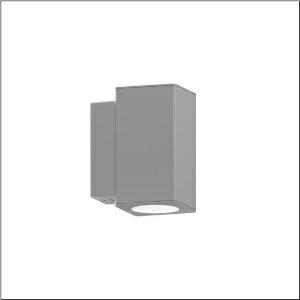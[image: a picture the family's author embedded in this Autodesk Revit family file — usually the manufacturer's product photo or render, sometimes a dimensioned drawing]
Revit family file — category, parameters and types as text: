
# Revit family: cl_31_wand_5cl563623
name_source: partatom
category: Lighting Fixtures
units: mm (PartAtom-declared; Revit-internal decimal feet)

## family parameters
Cut with Voids When Loaded = No
Host = Face
Light Source = No
Part Type = Normal
Room Calculation Point = No
Round Connector Dimension = Use Diameter
Shared = No

## types (1)
- --- (1 x LED, 600 lm, 5.4 W, 3000K)
    Apparent Load = 5 VA
    CIE Flux Codes = 98 100 100 50 100
    Color Rendering = 80
    Color Temperature = 3000K
    Default Elevation = 1800 mm
    Description = CL 31 Wall, wall luminaire, primary light control with reflector, of aluminium, primary optical cover: cover panel, of glass, transparent, light emission: up/down distribution, primary light characteristic: symmetric, installation type: surface-mounted, for 2x LED, rated luminous flux: 300lm, luminous efficacy: 110lm/W, light colour: 830, colour temperature: 3000K, control gear: ECG DALI, with terminal, 5-pole, max. 2.5mm², mains connection: 220..240V, AC, 50/60Hz, rated input power: 5.5W, luminaire housing, square, of aluminium, powder-coated, Siteco® metallic grey, length: 143mm, width: 100mm, height: 186mm, protection rating (complete): IP65, insulation class (complete): insulation class I (protective earthing), certification: CE, ENEC, impact resistance: IK08, permissible operating ambient temperature for outdoor applications: -20..+50°C, packaging unit: 1 piece
    Height = 186 mm
    Lamp = 1 x LED
    Lamp Light Flux = 600 lm
    Lamp Power = 5.4 W
    Lamp count = 1
    Length = 100 mm  [stored 0.328084 ft]
    Luminous efficacy = 111 lm/W
    Manufacturer = Siteco
    ModVariant = No
    Model = 5CL563623
    Mounting Place = Wall
    Mounting Type = Surface mounted
    Number of Poles = 1
    OnlyDefault = Yes
    Power Factor = 1
    Product Name = CL 31 Wand
    Product group = wall luminaire
    ProductGroupID = 2002
    Protection Class = Protection class I
    Protection Degree = IP 65
    RLX_Detail_Level = 1
    RLX_Emergency_Light_Flux = 0 lm
    RLX_Emergency_Type = 0
    RLX_Emergency_Type_DB = No
    RlxData = <blob elided: 40317 chars, md5=c458680a>
    Socket = socket
    Standby Power = 0 W
    System Light Flux = 600 lm
    System Power = 5 W
    Type Comments = factory setting: luminous flux: 100 % | dim-lin: 254 | 135 mA
    Type Image = l_1006895.jpg
    URL = http://relux.com
    VarID = @adj_148521
    Voltage = 0 V
    Weight = 0.00 kg
    Width = 143 mm

note: [stored X ft] marks values corroborated as IEEE doubles in the binary element streams (Revit-internal decimal feet)

## geometry (parser evidence)
native form markers: Blend x4, Sweep x10
no freeform markers — native parametric forms only
